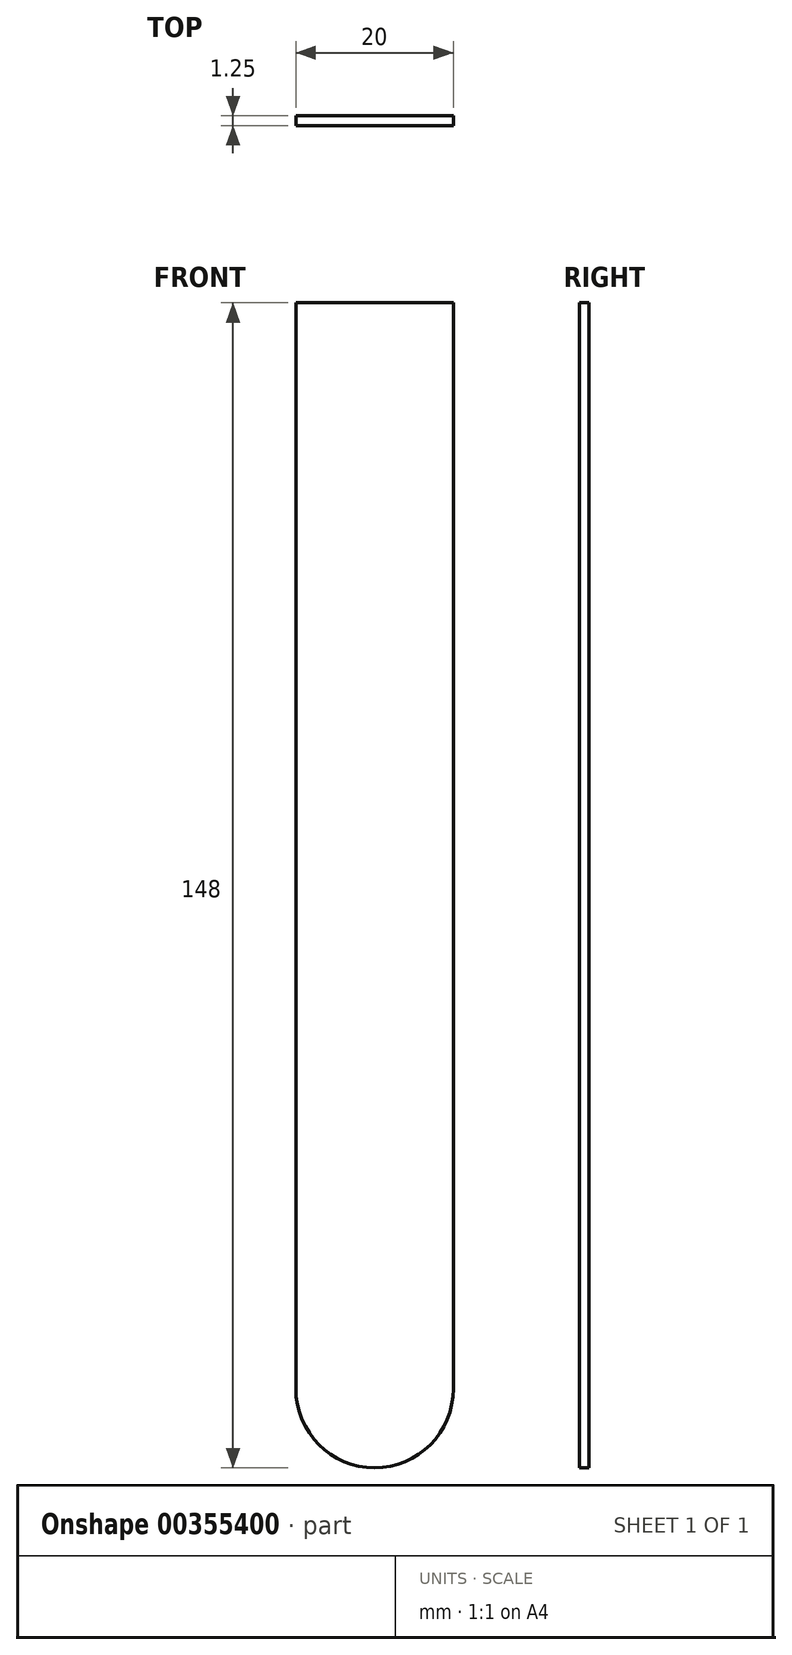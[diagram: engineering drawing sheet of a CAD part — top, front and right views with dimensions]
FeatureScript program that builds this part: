
annotation { "Feature Type Name" : "Feature", "Feature Type Description" : "" }
export const myFeature = defineFeature(function(context is Context, id is Id, definition is map)
    precondition{}
    {
        {
            var Q0;
            Q0=qCreatedBy(makeId("Front.planeOp"),FACE);
            var sketch = newSketch(context, id + "F0", { "sketchPlane" : qUnion([Q0])});
            skLineSegment(sketch, "E0.bottom", {"start": v(-10, 69) * mm, "end": v(10, 69) * mm});
            skLineSegment(sketch, "E0.top", {"start": v(-10, -69) * mm, "end": v(10, -69) * mm});
            skLineSegment(sketch, "E0.left", {"start": v(-10, 69) * mm, "end": v(-10, -69) * mm});
            skLineSegment(sketch, "E0.right", {"start": v(10, 69) * mm, "end": v(10, -69) * mm});
            skPoint(sketch, "E0.middle", {"position": v(0, 0) * mm});
            skArc(sketch, "E1", {"start": v(-10, -69) * mm, "mid": v(0, -79) * mm, "end": v(10, -69) * mm});
            skSolve(sketch);
        }
        {
            var Q0;
            Q0 = qSketchRegion(id + "F0", true);
            extrude(context, id + "F1", {"entities" : qUnion([Q0]), "depth" : 1.25 * mm});
        }
    });
